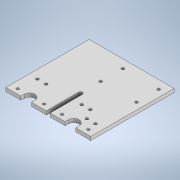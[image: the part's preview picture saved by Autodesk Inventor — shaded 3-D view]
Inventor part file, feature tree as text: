
AUTODESK INVENTOR PART (.ipt)
format: ipt  version: 2021 (Build 250183000, 183)  size: 183,808 bytes
history: native  units: mm
features: sketch x6, extrude x3, hole x3
ambient origin geometry x8: Origin, YZ Plane, XZ Plane, XY Plane, X Axis, Y Axis, Z Axis, Center Point
bodies: Solid1 (feature_tree)
feature tree (12):
  extrude  "Extrusion1"  Depth=116.2mm
  hole  "Hole1"  [1 undecoded]
  extrude  "Extrusion2"  Depth=50.0mm
  hole  "Hole2"  [1 undecoded]
  hole  "Hole3"  [1 undecoded]
  extrude  "Extrusion3"  Depth=10.0mm
  sketch  "Sketch1"  dims[d0=118.5mm d1=116.2mm]
  sketch  "Sketch2"  dims[d2=5.0mm d3=0.0mm d4=12.0mm]
  sketch  "Sketch3"  dims[d5=31.0mm d6=50.0mm]
  sketch  "Sketch4"  dims[d7=59.0mm]
  sketch  "Sketch5"  dims[d8=3.8mm d9=6.0mm d10=4.0mm d11=2.0mm d12=90.0deg d13=8.0mm d14=20.594885mm d18=5.05mm]
  sketch  "Sketch6"  dims[d19=45.0mm d20=10.0mm d21=0.0mm d22=32.0mm d23=12.0mm d24=12.0mm d25=12.0mm d26=14.5mm d27=18.5mm d28=12.0mm d29=12.0mm d30=3.8mm d31=6.0mm d32=4.0mm d33=2.0mm d34=90.0deg d35=8.0mm d36=20.594885mm d37=6.5mm d38=10.0mm d39=10.0mm d40=12.5mm d41=12.5mm d42=3.8mm d43=6.0mm d44=4.0mm d45=2.0mm d46=90.0deg d47=8.0mm d48=20.594885mm d49=15.0mm d50=15.0mm d51=4.5mm d52=4.5mm d53=10.0mm d54=10.0mm d55=0.0mm d56=0.0mm]
note: 3 required parameter values undecoded (feature->parameter linkage not recoverable at this tier; creation-order binding heuristic only, values carry confidence <= 0.55)
